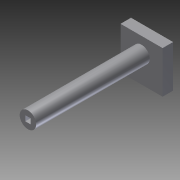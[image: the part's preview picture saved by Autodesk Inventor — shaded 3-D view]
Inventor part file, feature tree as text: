
AUTODESK INVENTOR PART (.ipt)
format: ipt  version: 2011 (Build 150239000, 239)  size: 110,592 bytes
history: native  units: in
note: dims shown in document units (in); Inventor stores cm internally (conversion verified against a paired STEP export)
features: extrude x5, sketch x5
ambient origin geometry x8: Origin, YZ Plane, XZ Plane, XY Plane, X Axis, Y Axis, Z Axis, Center Point
bodies: Solid1 (feature_tree)
feature tree (10):
  extrude  "Extrusion1"  Depth=5.9in TaperAngle=0.0deg
  extrude  "Extrusion2"  Depth=0.5in TaperAngle=0.0deg
  extrude  "Extrusion3"  Depth=1.0in
  extrude  "Extrusion4"  Depth=2.0in
  extrude  "Extrusion5"  Depth=0.25in TaperAngle=0.0deg
  sketch  "Sketch1"  dims[d0=0.78in d1=5.9in d2=0.0in]
  sketch  "Sketch2"  dims[d3=0.25in d4=0.5in d5=0.0in]
  sketch  "Sketch3"  dims[d6=1.0in d7=1.0in]
  sketch  "Sketch4"  dims[d8=2.0in d9=2.0in]
  sketch  "Sketch5"  dims[d10=0.5in d11=0.0in d12=0.25in d13=0.0in d14=2.0in d15=0.5in d16=0.0in]
